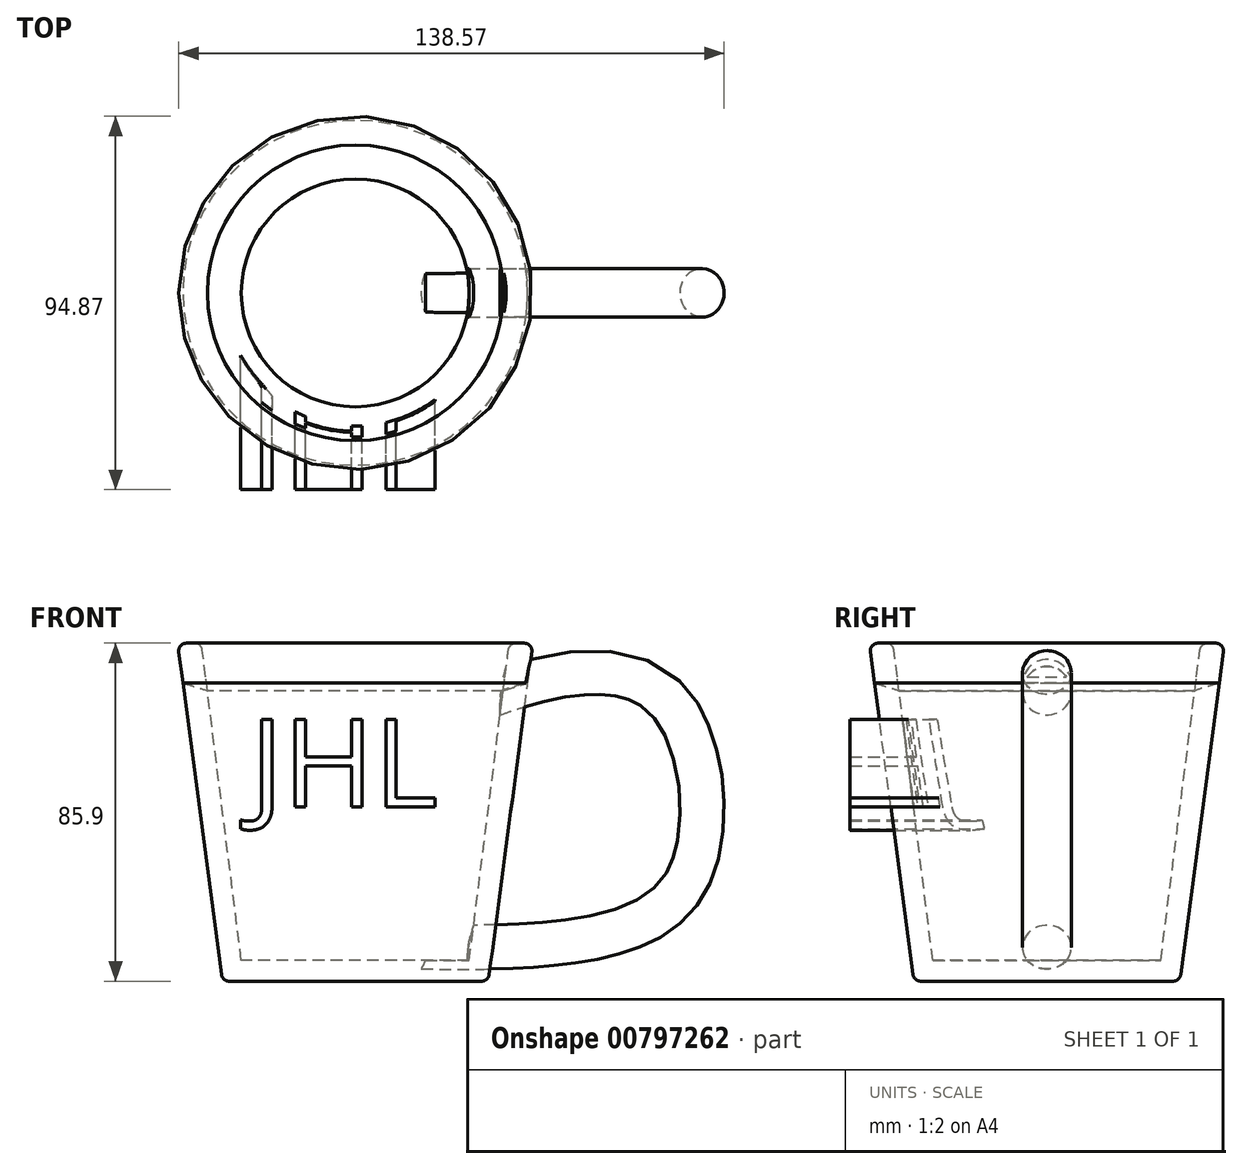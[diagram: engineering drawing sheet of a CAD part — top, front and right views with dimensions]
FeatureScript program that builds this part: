
annotation { "Feature Type Name" : "Feature", "Feature Type Description" : "" }
export const myFeature = defineFeature(function(context is Context, id is Id, definition is map)
    precondition{}
    {
        {
            var Q0;
            Q0=qCreatedBy(makeId("Front.planeOp"),FACE);
            var sketch = newSketch(context, id + "F0", { "sketchPlane" : qUnion([Q0])});
            skLineSegment(sketch, "E0", {"start": v(0, 50.7) * mm, "end": v(0, -65.6) * mm});
            skLineSegment(sketch, "E1", {"start": v(-6.03, -57.57) * mm, "end": v(33.8, -57.57) * mm});
            skLineSegment(sketch, "E2", {"start": v(33.8, -57.57) * mm, "end": v(45.15, 28.33) * mm});
            skLineSegment(sketch, "E3", {"start": v(45.15, 28.33) * mm, "end": v(39.1, 28.33) * mm});
            skFitSpline(sketch, "E4", {"points": [v(0, 0) * mm, v(54.85, 20.42) * mm, v(81.65, 10.72) * mm, v(83.6, -32.83) * mm, v(52.67, -47.63) * mm, v(19.45, -48.9) * mm], "startDerivative": vector(237.11, 113.16) * mm, "endDerivative": vector(-174.64, 1.36) * mm});
            skLineSegment(sketch, "E5", {"start": v(-6.88, -52.27) * mm, "end": v(28.96, -52.27) * mm});
            skLineSegment(sketch, "E6", {"start": v(28.96, -52.27) * mm, "end": v(38.35, 22.57) * mm});
            skLineSegment(sketch, "E7", {"start": v(38.35, 22.57) * mm, "end": v(-3.64, 22.57) * mm});
            skLineSegment(sketch, "E8", {"start": v(39.1, 28.33) * mm, "end": v(38, 19.75) * mm});
            skSolve(sketch);
        }
        {
            var Q0;
            {var subQ0=sQuery(id+"F0.wireOp",EDGE,"E2");Q0=makeQuery(id+"F0.imprint","IMPRINT",FACE,{"disambiguationData":[TD([[makeQuery(id+"F0.imprint","IMPRINT",EDGE,{"derivedFrom":subQ0}),1.0]])]});}
            var Q1;
            {var subQ6=sQuery(id+"F0.wireOp",EDGE,"E1");var subQ9=sQuery(id+"F0.wireOp",EDGE,"E0");var subQ10=makeQuery(id+"F0.imprint","INTERSECT",VERTEX,{"derivedFrom":[subQ9,subQ6]});Q1=makeQuery(id+"F0.imprint","IMPRINT",FACE,{"disambiguationData":[TD([[makeQuery(id+"F0.imprint","IMPRINT",EDGE,{"disambiguationData":[TD([[subQ10,1.0]])],"derivedFrom":subQ9}),1.0]])]});}
            var Q2;
            Q2=sQuery(id+"F0.wireOp",EDGE,"E0");
            revolve(context, id + "F1", {"surfaceOperationType" : NewSurfaceOperationType.NEW, "entities" : qUnion([Q0, Q1]), "axis" : qUnion([Q2]), "revolveType" : RevolveType.FULL});
        }
        {
            var Q0;
            Q0=qCreatedBy(makeId("Right.planeOp"),FACE);
            var sketch = newSketch(context, id + "F2", { "sketchPlane" : qUnion([Q0])});
            skCircle(sketch, "E9", {"center": v(0, 0) * mm, "radius": 6.2 * mm});
            skSolve(sketch);
        }
        {
            var Q0;
            Q0=makeQuery(id+"F2.imprint","IMPRINT",FACE,{"disambiguationData":[TD([[makeQuery(id+"F2.imprint","IMPRINT",EDGE,{"derivedFrom":sQuery(id+"F2.wireOp",EDGE,"E9")}),1.0]])]});
            var Q1;
            Q1=sQuery(id+"F0.wireOp",EDGE,"E4");
            sweep(context, id + "F3", {"profiles" : qUnion([Q0]), "path" : qUnion([Q1])});
        }
        {
            var Q0;
            Q0=qCreatedBy(makeId("Front.planeOp"),FACE);
            var sketch = newSketch(context, id + "F4", { "sketchPlane" : qUnion([Q0])});
            skText(sketch, "E10", { "text": "JHL", "fontName": "OpenSans-Regular.ttf"});
            const initialGuessF4  = {"E10": [-0.02665, -0.01334, 1, 0, 0.0225]};
            skSetInitialGuess(sketch, initialGuessF4);
            skSolve(sketch);
        }
        {
            var Q0;
            Q0 = qSketchRegion(id + "F4", true);
            extrude(context, id + "F5", {"entities" : qUnion([Q0]), "depth" : 50 * mm, "offsetDistance" : 25 * mm});
        }
        {
            var Q0;
            {var subQ0=sQuery(id+"F0.wireOp",EDGE,"E4");var subQ1=sQuery(id+"F0.wireOp",EDGE,"E0");var subQ2=makeQuery(id+"F0.imprint","INTERSECT",VERTEX,{"derivedFrom":[subQ1,subQ0]});Q0=makeQuery(id+"F0.imprint","IMPRINT",FACE,{"disambiguationData":[TD([[makeQuery(id+"F0.imprint","IMPRINT",EDGE,{"disambiguationData":[TD([[subQ2,1.0]])],"derivedFrom":subQ1}),1.0]])]});}
            var Q1;
            {var subQ6=sQuery(id+"F0.wireOp",EDGE,"E3");Q1=makeQuery(id+"F0.imprint","IMPRINT",FACE,{"disambiguationData":[TD([[makeQuery(id+"F0.imprint","IMPRINT",EDGE,{"derivedFrom":subQ6}),1.0]])]});}
            var Q2;
            {var subQ3=sQuery(id+"F0.wireOp",EDGE,"E0");var subQ5=sQuery(id+"F0.wireOp",EDGE,"E4");var subQ7=makeQuery(id+"F0.imprint","INTERSECT",VERTEX,{"derivedFrom":[subQ3,subQ5]});Q2=makeQuery(id+"F0.imprint","IMPRINT",FACE,{"disambiguationData":[TD([[makeQuery(id+"F0.imprint","IMPRINT",EDGE,{"disambiguationData":[TD([[subQ7,-1.0]])],"derivedFrom":subQ3}),1.0]])]});}
            var Q3;
            Q3=sQuery(id+"F0.wireOp",EDGE,"E0");
            revolve(context, id + "F6", {"surfaceOperationType" : NewSurfaceOperationType.NEW, "entities" : qUnion([Q0, Q1, Q2]), "axis" : qUnion([Q3]), "revolveType" : RevolveType.FULL});
        }
        {
            var Q0;
            Q0=makeQuery(id+"F6.opRevolve","SWEPT_BODY",BODY,{"disambiguationData":[OSD([sQuery(id+"F0.wireOp",EDGE,"E0"),sQuery(id+"F0.wireOp",EDGE,"Sh360DpM-GMgO-S2Cq-0zd9-WutZmoWUW7xR"),sQuery(id+"F0.wireOp",EDGE,"95pBun5h-fh1O-nM6e-Var8-gpQ7p3bvV8DJ"),sQuery(id+"F0.wireOp",EDGE,"E7")])]});
            var Q1;
            Q1=makeQuery(id+"F5.opExtrude","SWEPT_BODY",BODY,{"disambiguationData":[OSD([sQuery(id+"F4.wireOp",EDGE,"E10.sketch_text.stroke-0"),sQuery(id+"F4.wireOp",EDGE,"E10.sketch_text.stroke-1"),sQuery(id+"F4.wireOp",EDGE,"E10.sketch_text.stroke-2"),sQuery(id+"F4.wireOp",EDGE,"E10.sketch_text.stroke-3"),sQuery(id+"F4.wireOp",EDGE,"E10.sketch_text.stroke-4"),sQuery(id+"F4.wireOp",EDGE,"E10.sketch_text.stroke-5"),sQuery(id+"F4.wireOp",EDGE,"E10.sketch_text.stroke-6"),sQuery(id+"F4.wireOp",EDGE,"E10.sketch_text.stroke-7"),sQuery(id+"F4.wireOp",EDGE,"E10.sketch_text.stroke-8"),sQuery(id+"F4.wireOp",EDGE,"E10.sketch_text.stroke-9")])]});
            var Q2;
            Q2=makeQuery(id+"F5.opExtrude","SWEPT_BODY",BODY,{"disambiguationData":[OSD([sQuery(id+"F4.wireOp",EDGE,"E10.sketch_text.stroke-10"),sQuery(id+"F4.wireOp",EDGE,"E10.sketch_text.stroke-11"),sQuery(id+"F4.wireOp",EDGE,"E10.sketch_text.stroke-12"),sQuery(id+"F4.wireOp",EDGE,"E10.sketch_text.stroke-13"),sQuery(id+"F4.wireOp",EDGE,"E10.sketch_text.stroke-14"),sQuery(id+"F4.wireOp",EDGE,"E10.sketch_text.stroke-15"),sQuery(id+"F4.wireOp",EDGE,"E10.sketch_text.stroke-16"),sQuery(id+"F4.wireOp",EDGE,"E10.sketch_text.stroke-17"),sQuery(id+"F4.wireOp",EDGE,"E10.sketch_text.stroke-18"),sQuery(id+"F4.wireOp",EDGE,"E10.sketch_text.stroke-19"),sQuery(id+"F4.wireOp",EDGE,"E10.sketch_text.stroke-20"),sQuery(id+"F4.wireOp",EDGE,"E10.sketch_text.stroke-21")])]});
            var Q3;
            Q3=makeQuery(id+"F5.opExtrude","SWEPT_BODY",BODY,{"disambiguationData":[OSD([sQuery(id+"F4.wireOp",EDGE,"E10.sketch_text.stroke-22"),sQuery(id+"F4.wireOp",EDGE,"E10.sketch_text.stroke-23"),sQuery(id+"F4.wireOp",EDGE,"E10.sketch_text.stroke-24"),sQuery(id+"F4.wireOp",EDGE,"E10.sketch_text.stroke-25"),sQuery(id+"F4.wireOp",EDGE,"E10.sketch_text.stroke-26"),sQuery(id+"F4.wireOp",EDGE,"E10.sketch_text.stroke-27")])]});
            var Q4;
            Q4=makeQuery(id+"F3.opSweep","SWEPT_BODY",BODY,{"disambiguationData":[OSD([sQuery(id+"F0.wireOp",EDGE,"E4"),sQuery(id+"F2.wireOp",EDGE,"E9")])]});
            booleanBodies(context, id + "F7", {"operationType" : BooleanOperationType.SUBTRACTION, "tools" : qUnion([Q0]), "targets" : qUnion([Q1, Q2, Q3, Q4])});
        }
        {
            var Q0;
            Q0=makeQuery(id+"F6.opRevolve","SWEPT_EDGE",EDGE,{"disambiguationData":[OSD([sQuery(id+"F0.wireOp",EDGE,"E3"),sQuery(id+"F0.wireOp",EDGE,"Sh360DpM-GMgO-S2Cq-0zd9-WutZmoWUW7xR")])]});
            var Q1;
            Q1=makeQuery(id+"F1.opRevolve","SWEPT_FACE",FACE,{"disambiguationData":[OSD([sQuery(id+"F0.wireOp",EDGE,"E1")])]});
            fillet(context, id + "F8", {"entities" : qUnion([Q0, Q1]), "radius" : 2 * mm, "tangentPropagation" : true, "allowEdgeOverflow" : false});
        }
        {
            var Q0;
            {var subQ6=sQuery(id+"F0.wireOp",EDGE,"E3");Q0=makeQuery(id+"F0.imprint","IMPRINT",FACE,{"disambiguationData":[TD([[makeQuery(id+"F0.imprint","IMPRINT",EDGE,{"derivedFrom":subQ6}),1.0]])]});}
            var Q1;
            Q1=makeQuery(id+"F1.opRevolve","SWEPT_FACE",FACE,{"disambiguationData":[OSD([sQuery(id+"F0.wireOp",EDGE,"E6")])]});
            revolve(context, id + "F9", {"surfaceOperationType" : NewSurfaceOperationType.NEW, "entities" : qUnion([Q0]), "axis" : qUnion([Q1]), "revolveType" : RevolveType.FULL});
        }
        {
            var Q0;
            {var subQ3=sQuery(id+"F0.wireOp",EDGE,"E0");var subQ5=sQuery(id+"F0.wireOp",EDGE,"E4");var subQ6=makeQuery(id+"F0.imprint","INTERSECT",VERTEX,{"derivedFrom":[subQ3,subQ5]});Q0=makeQuery(id+"F0.imprint","IMPRINT",FACE,{"disambiguationData":[TD([[makeQuery(id+"F0.imprint","IMPRINT",EDGE,{"disambiguationData":[TD([[subQ6,-1.0]])],"derivedFrom":subQ3}),1.0]])]});}
            var Q1;
            Q1=makeQuery(id+"F1.opRevolve","SWEPT_FACE",FACE,{"disambiguationData":[OSD([sQuery(id+"F0.wireOp",EDGE,"E2")])]});
            revolve(context, id + "F10", {"surfaceOperationType" : NewSurfaceOperationType.NEW, "entities" : qUnion([Q0]), "axis" : qUnion([Q1]), "revolveType" : RevolveType.FULL});
        }
        {
            var Q0;
            Q0=makeQuery(id+"F10.opRevolve","SWEPT_BODY",BODY,{"disambiguationData":[OSD([sQuery(id+"F0.wireOp",EDGE,"E0"),sQuery(id+"F0.wireOp",EDGE,"E4"),sQuery(id+"F0.wireOp",EDGE,"E5"),sQuery(id+"F0.wireOp",EDGE,"E6")])]});
            var Q1;
            Q1=makeQuery(id+"F7.opBoolean","SPLIT",BODY,{"disambiguationData":[OD(1.0)],"derivedFrom":makeQuery(id+"F3.opSweep","SWEPT_BODY",BODY,{"disambiguationData":[OSD([sQuery(id+"F0.wireOp",EDGE,"E4"),sQuery(id+"F2.wireOp",EDGE,"E9")])]})});
            booleanBodies(context, id + "F11", {"operationType" : BooleanOperationType.SUBTRACTION, "tools" : qUnion([Q0]), "targets" : qUnion([Q1])});
        }
        {
            var Q0;
            Q0=makeQuery(id+"F9.opRevolve","SWEPT_EDGE",EDGE,{"disambiguationData":[OSD([sQuery(id+"F0.wireOp",EDGE,"E2"),sQuery(id+"F0.wireOp",EDGE,"E3")])]});
            var Q1;
            Q1=makeQuery(id+"F9.opRevolve","SWEPT_EDGE",EDGE,{"disambiguationData":[OSD([sQuery(id+"F0.wireOp",EDGE,"E3"),sQuery(id+"F0.wireOp",EDGE,"E8")])]});
            fillet(context, id + "F12", {"entities" : qUnion([Q0, Q1]), "radius" : 2 * mm, "tangentPropagation" : true, "allowEdgeOverflow" : false});
        }
    });
